# Revit family: Curtain_Door-Bifold-CRL-Aluminum-S55-Even_Panel_Bifolding
name_source: partatom
category: Doors
revit_build: Autodesk Revit Architecture 2015 (Build: 20140606_1530(x64)
units: mm (PartAtom-declared; Revit-internal decimal feet)

## types (1)
- 8 Panel Even Bi-Fold
    Assembly Code = B2030500
    Description = Monterey Bi-Folding Glass Wall with 8 Panels
    Function = Exterior
    Glass = Glass - C.R. Laurence - Clear Glazing
    Hardware Finish = Metal - C.R. Laurence - Clear Anodized – Aluminum
    Manufacturer = C.R. Laurence - U.S. Aluminum
    Material Note = Custom paint is available please contact vendor for more information
    Model = S55
    Panel = Metal - C.R. Laurence - Clear Anodized – Aluminum
    Product Documentation Link = http://www.crl-arch.com
    Product Page URL = http://www.crl-arch.com
    Product data url = https://bimobject.com
    Thickness = 2 5/16"
    URL = http://www.crl-arch.com

## geometry (parser evidence)
native form markers: Blend x4, Sweep x15
no freeform markers — native parametric forms only
